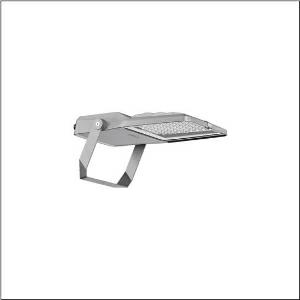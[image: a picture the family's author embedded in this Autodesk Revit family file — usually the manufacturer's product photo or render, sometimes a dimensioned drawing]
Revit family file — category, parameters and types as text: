
# Revit family: floodlight_fl_21_iq_mini___pl43_5xa7771c4a1a_6230
name_source: partatom
category: Lighting Fixtures
units: mm (PartAtom-declared; Revit-internal decimal feet)

## family parameters
Cut with Voids When Loaded = No
Host = Face
Light Source = No
Part Type = Normal
Room Calculation Point = No
Round Connector Dimension = Use Diameter
Shared = No

## types (1)
- --- (1 x LED, 13050 lm, 87.2 W, 4000K)
    Apparent Load = 87 VA
    CIE Flux Codes = 27 78 99 100 100
    Color Rendering = 70
    Color Temperature = 4000K
    Default Elevation = 1800 mm
    Description = Floodlight FL 21 iQ mini, floodlight, primary light control with lens, of PMMA, primary optical cover: protective disc, of toughened safety glass, transparent, light distribution: PL43, light emission: direct distribution, installation type: surface-mounted, LED, High Power LED, rated luminous flux: 13.050lm, luminous efficacy: 150lm/W, light colour: 740, colour temperature: 4000K, control gear: iQ Comfort/DALI, control: Auto-Match, Temp-Guard, Lumen-Switch, Night-Set, Smart-Wire, Light-Fading, Desk-Remote (wireless, voltage-free reading and setting of iQ features in the workshop via application-optimized NFC function/RFID function), optimised constant luminous flux control (CLO 2.0), with terminal, 6-pole, mains connection: 220..240V, AC, 50/60Hz, start of lifetime: 87W, end of service life: 92W, reduction: 40W, luminaire housing, of diecast aluminium, powder-coated, Siteco® metallic grey (DB 702S), corrosivity category C5 mid according to DIN EN ISO 12944, suitable for swimming pools, chlorine-resistant, sealing non-destructively replaceable, mounting bracket, of steel, galvanised, powder-coated, Siteco® metallic grey (DB 702S), protection rating (complete): IP66, insulation class (complete): insulation class II (safety insulation), certification: CE, ENEC, VDE, protection symbol: D, impact resistance: IK08, permissible operating ambient temperature: -40..+40°C, permissible operating ambient temperature for outdoor applications: -40..+50°C, standard: DIN EN 12944, LABS conformity tested according to VDMA 24364:2018-05, packaging unit: 1 piece

Light Distribution: PL43
    Height = 70 mm
    Lamp = 1 x LED
    Lamp Light Flux = 13050 lm
    Lamp Power = 87.2 W
    Lamp count = 1
    Length = 485 mm
    Luminous efficacy = 150 lm/W
    Manufacturer = Siteco
    ModVariant = No
    Model = 5XA7771C4A1A
    Number of Poles = 1
    OnlyDefault = Yes
    Power Factor = 1
    Product Name = Floodlight FL 21 iQ mini | PL43
    Product group = floodlight | pylon annexe
    ProductGroupID = 6200
    Protection Class = Protection class II
    Protection Degree = IP 66
    RLX_Detail_Level = 1
    RLX_Emergency_Light_Flux = 0 lm
    RLX_Emergency_Type = 0
    RLX_Emergency_Type_DB = No
    RlxData = <blob elided: 96173 chars, md5=1239472f>
    Socket = socket
    Standby Power = 0 W
    System Light Flux = 13050 lm
    System Power = 87 W
    Type Comments = factory setting: luminous flux: 100 % | dim-lin: 254 | 456 mA
    Type Image = l_1006845.jpg
    URL = http://relux.com
    VarID = @adj_161942
    Voltage = 0 V
    Weight = 0.00 kg
    Width = 337 mm

## geometry (parser evidence)
native form markers: Blend x4, Sweep x11
no freeform markers — native parametric forms only
